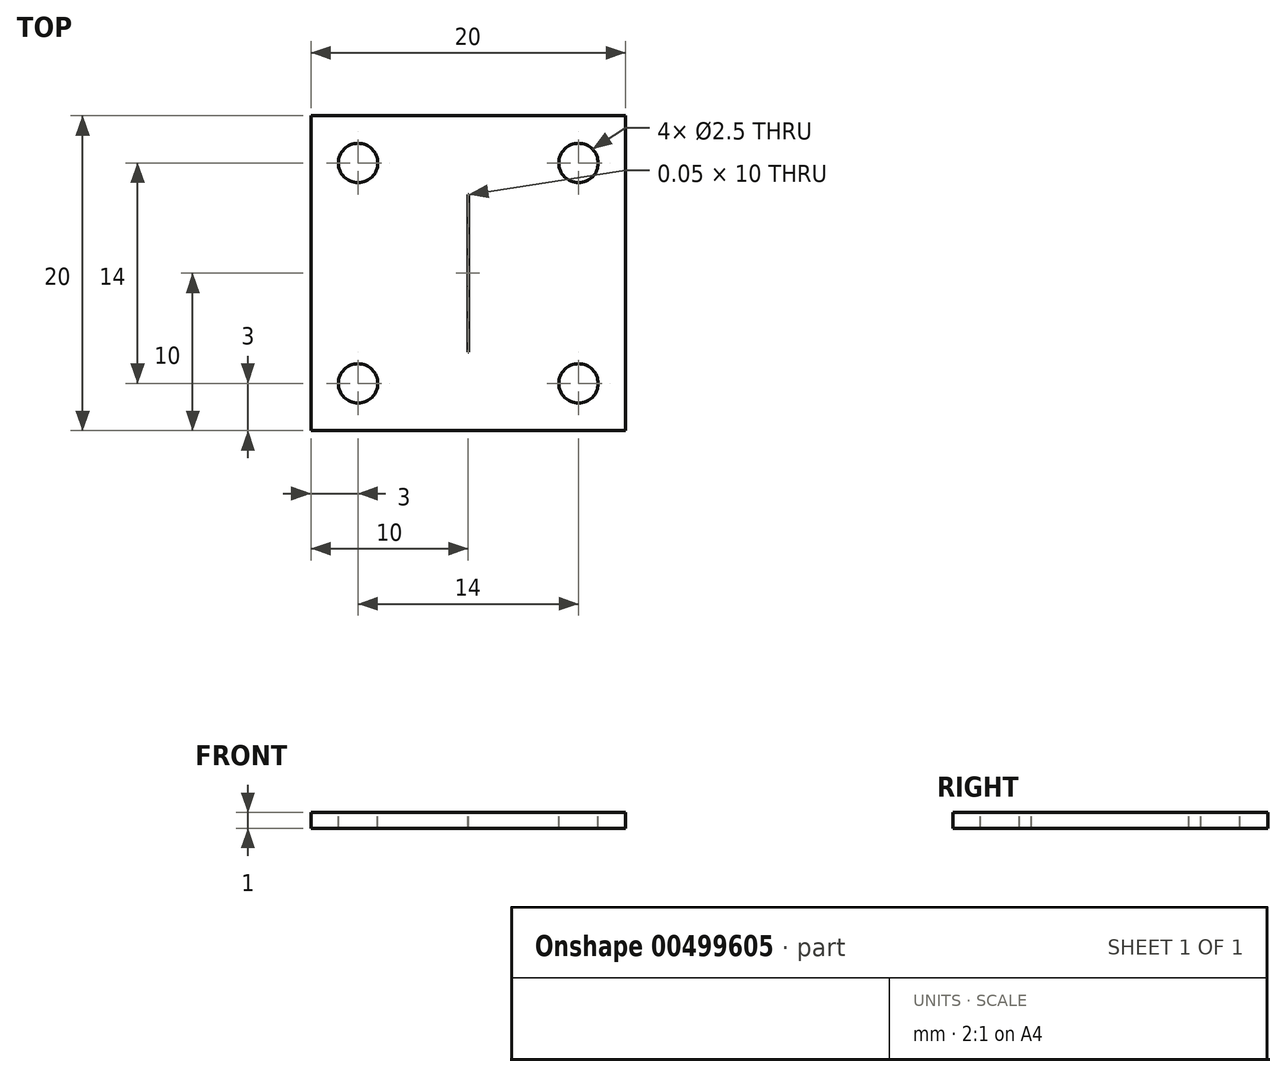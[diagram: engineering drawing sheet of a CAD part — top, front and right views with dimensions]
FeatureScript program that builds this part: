
annotation { "Feature Type Name" : "Feature", "Feature Type Description" : "" }
export const myFeature = defineFeature(function(context is Context, id is Id, definition is map)
    precondition{}
    {
        {
            var Q0;
            Q0=qCreatedBy(makeId("Top.planeOp"),FACE);
            var sketch = newSketch(context, id + "F0", { "sketchPlane" : qUnion([Q0])});
            skLineSegment(sketch, "E0.bottom", {"start": v(-10, 10) * mm, "end": v(10, 10) * mm});
            skLineSegment(sketch, "E0.top", {"start": v(-10, -10) * mm, "end": v(10, -10) * mm});
            skLineSegment(sketch, "E0.left", {"start": v(-10, 10) * mm, "end": v(-10, -10) * mm});
            skLineSegment(sketch, "E0.right", {"start": v(10, 10) * mm, "end": v(10, -10) * mm});
            skPoint(sketch, "E0.middle", {"position": v(0, 0) * mm});
            skSolve(sketch);
        }
        {
            var Q0;
            Q0=makeQuery(id+"F0.imprint","IMPRINT",FACE,{"disambiguationData":[TD([[makeQuery(id+"F0.imprint","IMPRINT",EDGE,{"derivedFrom":sQuery(id+"F0.wireOp",EDGE,"E0.bottom")}),-1.0]])]});
            extrude(context, id + "F1", {"entities" : qUnion([Q0]), "depth" : 1 * mm});
        }
        {
            var Q0;
            Q0=makeQuery(id+"F1.opExtrude","CAP_FACE",FACE,{"disambiguationData":[OSD([sQuery(id+"F0.wireOp",EDGE,"E0.bottom"),sQuery(id+"F0.wireOp",EDGE,"E0.top"),sQuery(id+"F0.wireOp",EDGE,"E0.left"),sQuery(id+"F0.wireOp",EDGE,"E0.right")])],"isStart":false});
            var sketch = newSketch(context, id + "F2", { "sketchPlane" : qUnion([Q0])});
            skLineSegment(sketch, "E1.bottom", {"start": v(-0.02, 5) * mm, "end": v(0.03, 5) * mm});
            skLineSegment(sketch, "E1.top", {"start": v(-0.02, -5) * mm, "end": v(0.03, -5) * mm});
            skLineSegment(sketch, "E1.left", {"start": v(-0.02, 5) * mm, "end": v(-0.02, -5) * mm});
            skLineSegment(sketch, "E1.right", {"start": v(0.03, 5) * mm, "end": v(0.03, -5) * mm});
            skPoint(sketch, "E1.middle", {"position": v(0, 0) * mm});
            skSolve(sketch);
        }
        {
            var Q0;
            Q0=makeQuery(id+"F2.imprint","IMPRINT",FACE,{"disambiguationData":[TD([[makeQuery(id+"F2.imprint","IMPRINT",EDGE,{"derivedFrom":sQuery(id+"F2.wireOp",EDGE,"E1.bottom")}),-1.0]])]});
            extrude(context, id + "F3", {"entities" : qUnion([Q0]), "operationType" : NewBodyOperationType.REMOVE, "oppositeDirection" : true, "depth" : 25 * mm});
        }
        {
            var Q0;
            Q0=makeQuery(id+"F1.opExtrude","CAP_FACE",FACE,{"disambiguationData":[OSD([sQuery(id+"F0.wireOp",EDGE,"E0.bottom"),sQuery(id+"F0.wireOp",EDGE,"E0.top"),sQuery(id+"F0.wireOp",EDGE,"E0.left"),sQuery(id+"F0.wireOp",EDGE,"E0.right")])],"isStart":false});
            var sketch = newSketch(context, id + "F4", { "sketchPlane" : qUnion([Q0])});
            skPoint(sketch, "E2", {"position": v(7, -7) * mm});
            skLineSegment(sketch, "E3", {"start": v(0, 11.81) * mm, "end": v(0, -13.92) * mm});
            skLineSegment(sketch, "E4", {"start": v(12.6, 0) * mm, "end": v(-12.15, 0) * mm});
            skPoint(sketch, "E4.endSnap0", {"position": v(-10, 0) * mm});
            skPoint(sketch, "E5.MirrorP", {"position": v(7, 7) * mm});
            skPoint(sketch, "E6.MirrorP", {"position": v(-7, -7) * mm});
            skPoint(sketch, "E7.MirrorP", {"position": v(-7, 7) * mm});
            skSolve(sketch);
        }
        {
            var Q0;
            Q0=sQuery(id+"F4.wireOp",VERTEX,"E6.MirrorP");
            var Q1;
            Q1=sQuery(id+"F4.wireOp",VERTEX,"E2");
            var Q2;
            Q2=sQuery(id+"F4.wireOp",VERTEX,"E5.MirrorP");
            var Q3;
            Q3=sQuery(id+"F4.wireOp",VERTEX,"E7.MirrorP");
            var Q4;
            Q4=makeQuery(id+"F1.opExtrude","SWEPT_BODY",BODY,{"disambiguationData":[OSD([sQuery(id+"F0.wireOp",EDGE,"E0.bottom"),sQuery(id+"F0.wireOp",EDGE,"E0.top"),sQuery(id+"F0.wireOp",EDGE,"E0.left"),sQuery(id+"F0.wireOp",EDGE,"E0.right")])]});
            hole(context, id + "F5", {"style" : HoleStyle.SIMPLE, "endStyle" : HoleEndStyle.THROUGH, "standardTappedOrClearance" : lookupTablePath({ "standard" : "ISO", "engagement" : "75%", "pitch" : "0.5 mm", "size" : "M3", "type" : "Tapped" }), "standardBlindInLast" : lookupTablePath({ "standard" : "ISO", "engagement" : "75%", "pitch" : "0.5 mm", "size" : "M3", "type" : "Tapped" }), "holeDiameter" : 2.5 * mm, "showTappedDepth" : true, "isTappedThrough" : true, "tappedDepth" : 12 * mm, "tapClearance" : 3, "startFromSketch" : true, "locations" : qUnion([Q0, Q1, Q2, Q3]), "scope" : qUnion([Q4]), "majorDiameter" : 3 * mm});
        }
    });
